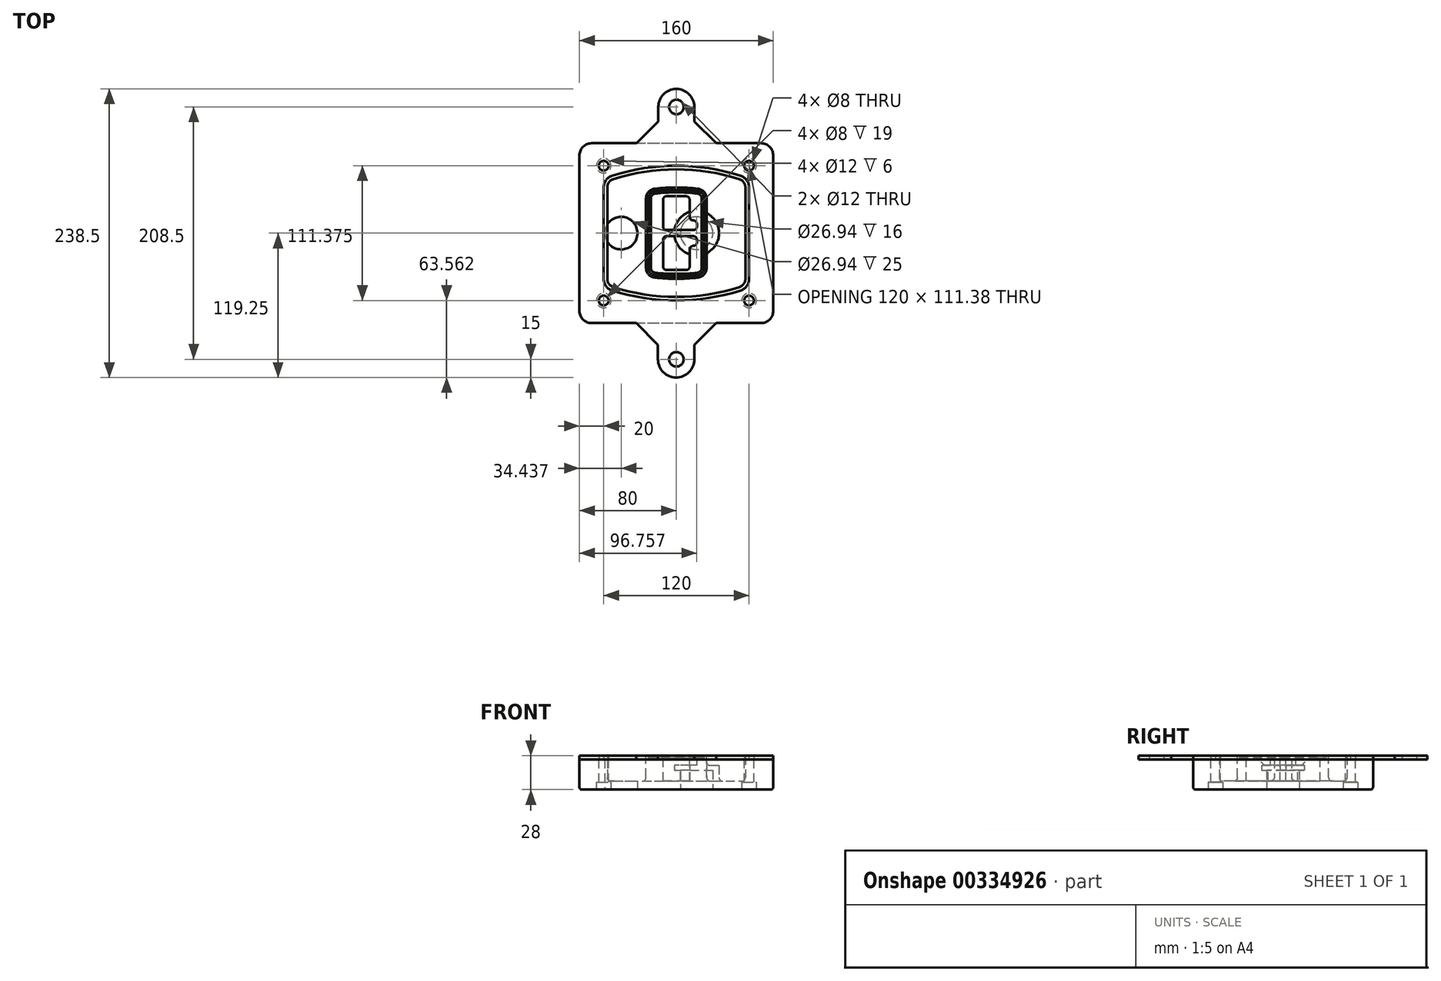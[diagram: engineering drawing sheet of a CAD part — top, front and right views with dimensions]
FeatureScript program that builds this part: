
annotation { "Feature Type Name" : "Feature", "Feature Type Description" : "" }
export const myFeature = defineFeature(function(context is Context, id is Id, definition is map)
    precondition{}
    {
        {
            var Q0;
            Q0=qCreatedBy(makeId("Top.planeOp"),FACE);
            var sketch = newSketch(context, id + "F0", { "sketchPlane" : qUnion([Q0])});
            skPoint(sketch, "E0.rect.middle", {"position": v(0, 0) * mm});
            skLineSegment(sketch, "E1.bottom", {"start": v(-70, -74.25) * mm, "end": v(70, -74.25) * mm});
            skLineSegment(sketch, "E1.top", {"start": v(-70, 74.25) * mm, "end": v(70, 74.25) * mm});
            skLineSegment(sketch, "E1.left", {"start": v(-80, -64.25) * mm, "end": v(-80, 64.25) * mm});
            skLineSegment(sketch, "E1.right", {"start": v(80, -64.25) * mm, "end": v(80, 64.25) * mm});
            skLineSegment(sketch, "E2", {"start": v(-80, 74.25) * mm, "end": v(80, -74.25) * mm, "construction": true});
            skLineSegment(sketch, "E3", {"start": v(80, 74.25) * mm, "end": v(-80, -74.25) * mm, "construction": true});
            skCircle(sketch, "E4", {"center": v(-60, 55.69) * mm, "radius": 4 * mm});
            skCircle(sketch, "E5", {"center": v(60, 55.69) * mm, "radius": 4 * mm});
            skCircle(sketch, "E6", {"center": v(60, -55.69) * mm, "radius": 4 * mm});
            skCircle(sketch, "E7", {"center": v(-60, -55.69) * mm, "radius": 4 * mm});
            skLineSegment(sketch, "E8", {"start": v(-60, 55.69) * mm, "end": v(60, 55.69) * mm, "construction": true});
            skLineSegment(sketch, "E9", {"start": v(60, 55.69) * mm, "end": v(60, -55.69) * mm, "construction": true});
            skLineSegment(sketch, "E10", {"start": v(60, -55.69) * mm, "end": v(-60, -55.69) * mm, "construction": true});
            skLineSegment(sketch, "E11", {"start": v(-60, -55.69) * mm, "end": v(-60, 55.69) * mm, "construction": true});
            skLineSegment(sketch, "E12", {"start": v(-60, 37.87) * mm, "end": v(-60, -37.87) * mm});
            skLineSegment(sketch, "E13", {"start": v(60, 37.87) * mm, "end": v(60, -37.87) * mm});
            skArc(sketch, "E14", {"start": v(53.05, 47.4) * mm, "mid": v(0, 55.69) * mm, "end": v(-53.05, 47.4) * mm});
            skArc(sketch, "E15", {"start": v(-53.05, -47.4) * mm, "mid": v(0, -55.69) * mm, "end": v(53.05, -47.4) * mm});
            skLineSegment(sketch, "E16", {"start": v(-60, 0) * mm, "end": v(60, 0) * mm, "construction": true});
            skPoint(sketch, "E17.visualSharp", {"position": v(-60, -45) * mm});
            skArc(sketch, "E17.filletArc", {"start": v(-60, -37.87) * mm, "mid": v(-58.08, -43.76) * mm, "end": v(-53.05, -47.4) * mm});
            skPoint(sketch, "E18.visualSharp", {"position": v(-60, 45) * mm});
            skArc(sketch, "E18.filletArc", {"start": v(-53.05, 47.4) * mm, "mid": v(-58.08, 43.76) * mm, "end": v(-60, 37.87) * mm});
            skPoint(sketch, "E19.visualSharp", {"position": v(60, 45) * mm});
            skArc(sketch, "E19.filletArc", {"start": v(60, 37.87) * mm, "mid": v(58.08, 43.76) * mm, "end": v(53.05, 47.4) * mm});
            skPoint(sketch, "E20.visualSharp", {"position": v(60, -45) * mm});
            skArc(sketch, "E20.filletArc", {"start": v(53.05, -47.4) * mm, "mid": v(58.08, -43.76) * mm, "end": v(60, -37.87) * mm});
            skPoint(sketch, "E21.visualSharp", {"position": v(-80, 74.25) * mm});
            skArc(sketch, "E21.filletArc", {"start": v(-70, 74.25) * mm, "mid": v(-77.07, 71.32) * mm, "end": v(-80, 64.25) * mm});
            skPoint(sketch, "E22.visualSharp", {"position": v(80, 74.25) * mm});
            skArc(sketch, "E22.filletArc", {"start": v(80, 64.25) * mm, "mid": v(77.07, 71.32) * mm, "end": v(70, 74.25) * mm});
            skPoint(sketch, "E23.visualSharp", {"position": v(80, -74.25) * mm});
            skArc(sketch, "E23.filletArc", {"start": v(70, -74.25) * mm, "mid": v(77.07, -71.32) * mm, "end": v(80, -64.25) * mm});
            skPoint(sketch, "E24.visualSharp", {"position": v(-80, -74.25) * mm});
            skArc(sketch, "E24.filletArc", {"start": v(-80, -64.25) * mm, "mid": v(-77.07, -71.32) * mm, "end": v(-70, -74.25) * mm});
            skArc(sketch, "E25.0", {"start": v(57, 37.87) * mm, "mid": v(55.66, 42) * mm, "end": v(52.14, 44.53) * mm});
            skLineSegment(sketch, "E25.1", {"start": v(57, 37.87) * mm, "end": v(57, -37.87) * mm});
            skArc(sketch, "E25.2", {"start": v(52.14, -44.53) * mm, "mid": v(55.66, -42) * mm, "end": v(57, -37.87) * mm});
            skArc(sketch, "E25.3", {"start": v(-52.14, -44.53) * mm, "mid": v(0, -52.69) * mm, "end": v(52.14, -44.53) * mm});
            skArc(sketch, "E25.4", {"start": v(-57, -37.87) * mm, "mid": v(-55.66, -42) * mm, "end": v(-52.14, -44.53) * mm});
            skArc(sketch, "E25.5", {"start": v(52.14, 44.53) * mm, "mid": v(0, 52.69) * mm, "end": v(-52.14, 44.53) * mm});
            skLineSegment(sketch, "E25.6", {"start": v(-57, 37.87) * mm, "end": v(-57, -37.87) * mm});
            skArc(sketch, "E25.7", {"start": v(-52.14, 44.53) * mm, "mid": v(-55.66, 42) * mm, "end": v(-57, 37.87) * mm});
            skArc(sketch, "E26.0", {"start": v(-54.27, 51.2) * mm, "mid": v(-61.31, 46.12) * mm, "end": v(-64, 37.87) * mm});
            skArc(sketch, "E26.1", {"start": v(54.27, 51.2) * mm, "mid": v(0, 59.69) * mm, "end": v(-54.27, 51.2) * mm});
            skArc(sketch, "E26.2", {"start": v(64, 37.87) * mm, "mid": v(61.31, 46.12) * mm, "end": v(54.27, 51.2) * mm});
            skLineSegment(sketch, "E26.3", {"start": v(64, 37.87) * mm, "end": v(64, -37.87) * mm});
            skArc(sketch, "E26.4", {"start": v(54.27, -51.2) * mm, "mid": v(61.31, -46.12) * mm, "end": v(64, -37.87) * mm});
            skLineSegment(sketch, "E26.5", {"start": v(-64, 37.87) * mm, "end": v(-64, -37.87) * mm});
            skArc(sketch, "E26.6", {"start": v(-54.27, -51.2) * mm, "mid": v(0, -59.69) * mm, "end": v(54.27, -51.2) * mm});
            skArc(sketch, "E26.7", {"start": v(-64, -37.87) * mm, "mid": v(-61.31, -46.12) * mm, "end": v(-54.27, -51.2) * mm});
            skSolve(sketch);
        }
        {
            var Q0;
            Q0=makeQuery(id+"F0.imprint","IMPRINT",FACE,{"disambiguationData":[TD([[makeQuery(id+"F0.imprint","IMPRINT",EDGE,{"derivedFrom":sQuery(id+"F0.wireOp",EDGE,"E1.bottom")}),1.0]])]});
            var Q1;
            Q1=makeQuery(id+"F0.imprint","IMPRINT",FACE,{"disambiguationData":[TD([[makeQuery(id+"F0.imprint","IMPRINT",EDGE,{"derivedFrom":sQuery(id+"F0.wireOp",EDGE,"E12")}),1.0]])]});
            var Q2;
            Q2=makeQuery(id+"F0.imprint","IMPRINT",FACE,{"disambiguationData":[TD([[makeQuery(id+"F0.imprint","IMPRINT",EDGE,{"derivedFrom":sQuery(id+"F0.wireOp",EDGE,"E25.0")}),1.0]])]});
            var Q3;
            Q3=makeQuery(id+"F0.imprint","IMPRINT",FACE,{"disambiguationData":[TD([[makeQuery(id+"F0.imprint","IMPRINT",EDGE,{"derivedFrom":sQuery(id+"F0.wireOp",EDGE,"E12")}),-1.0]])]});
            extrude(context, id + "F1", {"entities" : qUnion([Q0, Q1, Q2, Q3]), "oppositeDirection" : true, "depth" : 25 * mm});
        }
        {
            var Q0;
            Q0=makeQuery(id+"F0.imprint","IMPRINT",FACE,{"disambiguationData":[TD([[makeQuery(id+"F0.imprint","IMPRINT",EDGE,{"derivedFrom":sQuery(id+"F0.wireOp",EDGE,"E12")}),1.0]])]});
            extrude(context, id + "F2", {"entities" : qUnion([Q0]), "operationType" : NewBodyOperationType.ADD, "depth" : 3 * mm});
        }
        {
            var Q0;
            Q0=makeQuery(id+"F0.imprint","IMPRINT",FACE,{"disambiguationData":[TD([[makeQuery(id+"F0.imprint","IMPRINT",EDGE,{"derivedFrom":sQuery(id+"F0.wireOp",EDGE,"E25.0")}),1.0]])]});
            extrude(context, id + "F3", {"entities" : qUnion([Q0]), "operationType" : NewBodyOperationType.REMOVE, "oppositeDirection" : true, "depth" : 18 * mm});
        }
        {
            var Q0;
            Q0=makeQuery(id+"F2.opExtrude","CAP_FACE",FACE,{"disambiguationData":[OSD([sQuery(id+"F0.wireOp",EDGE,"E12"),sQuery(id+"F0.wireOp",EDGE,"E13"),sQuery(id+"F0.wireOp",EDGE,"E14"),sQuery(id+"F0.wireOp",EDGE,"E15"),sQuery(id+"F0.wireOp",EDGE,"E17.filletArc"),sQuery(id+"F0.wireOp",EDGE,"E18.filletArc"),sQuery(id+"F0.wireOp",EDGE,"E19.filletArc"),sQuery(id+"F0.wireOp",EDGE,"E20.filletArc"),sQuery(id+"F0.wireOp",EDGE,"E25.0"),sQuery(id+"F0.wireOp",EDGE,"E25.1"),sQuery(id+"F0.wireOp",EDGE,"E25.2"),sQuery(id+"F0.wireOp",EDGE,"E25.3"),sQuery(id+"F0.wireOp",EDGE,"E25.4"),sQuery(id+"F0.wireOp",EDGE,"E25.5"),sQuery(id+"F0.wireOp",EDGE,"E25.6"),sQuery(id+"F0.wireOp",EDGE,"E25.7")])],"isStart":false});
            var sketch = newSketch(context, id + "F4", { "sketchPlane" : qUnion([Q0])});
            skArc(sketch, "E27.0", {"start": v(-17.92, -36.65) * mm, "mid": v(0, -37.69) * mm, "end": v(17.92, -36.65) * mm});
            skArc(sketch, "E28.0", {"start": v(17.92, 36.65) * mm, "mid": v(0, 37.69) * mm, "end": v(-17.92, 36.65) * mm});
            skLineSegment(sketch, "E29", {"start": v(-25, 28.7) * mm, "end": v(-25, -28.7) * mm});
            skLineSegment(sketch, "E30", {"start": v(25, 28.7) * mm, "end": v(25, -28.7) * mm});
            skLineSegment(sketch, "E31", {"start": v(-25, 35.67) * mm, "end": v(25, 35.67) * mm, "construction": true});
            skLineSegment(sketch, "E32", {"start": v(-25, -35.67) * mm, "end": v(25, -35.67) * mm, "construction": true});
            skPoint(sketch, "E33.visualSharp", {"position": v(-25, 35.67) * mm});
            skArc(sketch, "E33.filletArc", {"start": v(-17.92, 36.65) * mm, "mid": v(-22.97, 34.03) * mm, "end": v(-25, 28.7) * mm});
            skPoint(sketch, "E34.visualSharp", {"position": v(25, 35.67) * mm});
            skArc(sketch, "E34.filletArc", {"start": v(25, 28.7) * mm, "mid": v(22.97, 34.03) * mm, "end": v(17.92, 36.65) * mm});
            skPoint(sketch, "E35.visualSharp", {"position": v(25, -35.67) * mm});
            skArc(sketch, "E35.filletArc", {"start": v(17.92, -36.65) * mm, "mid": v(22.97, -34.03) * mm, "end": v(25, -28.7) * mm});
            skPoint(sketch, "E36.visualSharp", {"position": v(-25, -35.67) * mm});
            skArc(sketch, "E36.filletArc", {"start": v(-25, -28.7) * mm, "mid": v(-22.97, -34.03) * mm, "end": v(-17.92, -36.65) * mm});
            skArc(sketch, "E37.0", {"start": v(52.14, 44.53) * mm, "mid": v(0, 52.69) * mm, "end": v(-52.14, 44.53) * mm});
            skArc(sketch, "E37.1", {"start": v(-52.14, 44.53) * mm, "mid": v(-55.66, 42) * mm, "end": v(-57, 37.87) * mm});
            skLineSegment(sketch, "E37.2", {"start": v(-57, 37.87) * mm, "end": v(-57, -37.87) * mm});
            skArc(sketch, "E37.3", {"start": v(-57, -37.87) * mm, "mid": v(-55.66, -42) * mm, "end": v(-52.14, -44.53) * mm});
            skArc(sketch, "E37.4", {"start": v(-52.14, -44.53) * mm, "mid": v(0, -52.69) * mm, "end": v(52.14, -44.53) * mm});
            skArc(sketch, "E37.5", {"start": v(52.14, -44.53) * mm, "mid": v(55.66, -42) * mm, "end": v(57, -37.87) * mm});
            skLineSegment(sketch, "E37.6", {"start": v(57, 37.87) * mm, "end": v(57, -37.87) * mm});
            skArc(sketch, "E37.7", {"start": v(57, 37.87) * mm, "mid": v(55.66, 42) * mm, "end": v(52.14, 44.53) * mm});
            skLineSegment(sketch, "E38.0", {"start": v(23, 28.7) * mm, "end": v(23, -28.7) * mm});
            skArc(sketch, "E38.1", {"start": v(17.7, -34.67) * mm, "mid": v(21.48, -32.7) * mm, "end": v(23, -28.7) * mm});
            skArc(sketch, "E38.2", {"start": v(-17.7, -34.67) * mm, "mid": v(0, -35.69) * mm, "end": v(17.7, -34.67) * mm});
            skArc(sketch, "E38.3", {"start": v(-23, -28.7) * mm, "mid": v(-21.48, -32.7) * mm, "end": v(-17.7, -34.67) * mm});
            skLineSegment(sketch, "E38.4", {"start": v(-23, 28.7) * mm, "end": v(-23, -28.7) * mm});
            skArc(sketch, "E38.5", {"start": v(23, 28.7) * mm, "mid": v(21.48, 32.7) * mm, "end": v(17.7, 34.67) * mm});
            skArc(sketch, "E38.6", {"start": v(-17.7, 34.67) * mm, "mid": v(-21.48, 32.7) * mm, "end": v(-23, 28.7) * mm});
            skArc(sketch, "E38.7", {"start": v(17.7, 34.67) * mm, "mid": v(0, 35.69) * mm, "end": v(-17.7, 34.67) * mm});
            skArc(sketch, "E39.0", {"start": v(21, 28.7) * mm, "mid": v(19.99, 31.37) * mm, "end": v(17.46, 32.68) * mm});
            skLineSegment(sketch, "E39.1", {"start": v(21, 28.7) * mm, "end": v(21, -28.7) * mm});
            skArc(sketch, "E39.2", {"start": v(17.46, -32.68) * mm, "mid": v(19.99, -31.37) * mm, "end": v(21, -28.7) * mm});
            skArc(sketch, "E39.3", {"start": v(-17.46, -32.68) * mm, "mid": v(0, -33.69) * mm, "end": v(17.46, -32.68) * mm});
            skArc(sketch, "E39.4", {"start": v(-21, -28.7) * mm, "mid": v(-19.99, -31.37) * mm, "end": v(-17.46, -32.68) * mm});
            skArc(sketch, "E39.5", {"start": v(17.46, 32.68) * mm, "mid": v(0, 33.69) * mm, "end": v(-17.46, 32.68) * mm});
            skLineSegment(sketch, "E39.6", {"start": v(-21, 28.7) * mm, "end": v(-21, -28.7) * mm});
            skArc(sketch, "E39.7", {"start": v(-17.46, 32.68) * mm, "mid": v(-19.99, 31.37) * mm, "end": v(-21, 28.7) * mm});
            skLineSegment(sketch, "E40", {"start": v(-25, 0) * mm, "end": v(25, 0) * mm, "construction": true});
            skLineSegment(sketch, "E41", {"start": v(-11, 5.5) * mm, "end": v(-11, 27.5) * mm});
            skLineSegment(sketch, "E42", {"start": v(-8, 30.5) * mm, "end": v(8, 30.5) * mm});
            skLineSegment(sketch, "E43", {"start": v(11, 27.5) * mm, "end": v(11, 13.5) * mm});
            skLineSegment(sketch, "E44", {"start": v(14, 10.5) * mm, "end": v(14, 10.5) * mm});
            skLineSegment(sketch, "E45", {"start": v(17, 7.5) * mm, "end": v(17, 5.5) * mm});
            skLineSegment(sketch, "E46", {"start": v(14, 2.5) * mm, "end": v(-8, 2.5) * mm});
            skPoint(sketch, "E47.visualSharp", {"position": v(-11, 30.5) * mm});
            skArc(sketch, "E47.filletArc", {"start": v(-8, 30.5) * mm, "mid": v(-10.12, 29.62) * mm, "end": v(-11, 27.5) * mm});
            skPoint(sketch, "E48.visualSharp", {"position": v(11, 30.5) * mm});
            skArc(sketch, "E48.filletArc", {"start": v(11, 27.5) * mm, "mid": v(10.12, 29.62) * mm, "end": v(8, 30.5) * mm});
            skPoint(sketch, "E49.visualSharp", {"position": v(11, 10.5) * mm});
            skArc(sketch, "E49.filletArc", {"start": v(11, 13.5) * mm, "mid": v(11.88, 11.38) * mm, "end": v(14, 10.5) * mm});
            skPoint(sketch, "E50.visualSharp", {"position": v(17, 10.5) * mm});
            skArc(sketch, "E50.filletArc", {"start": v(17, 7.5) * mm, "mid": v(16.12, 9.62) * mm, "end": v(14, 10.5) * mm});
            skPoint(sketch, "E51.visualSharp", {"position": v(17, 2.5) * mm});
            skArc(sketch, "E51.filletArc", {"start": v(14, 2.5) * mm, "mid": v(16.12, 3.38) * mm, "end": v(17, 5.5) * mm});
            skPoint(sketch, "E52.visualSharp", {"position": v(-11, 2.5) * mm});
            skArc(sketch, "E52.filletArc", {"start": v(-11, 5.5) * mm, "mid": v(-10.12, 3.38) * mm, "end": v(-8, 2.5) * mm});
            skLineSegment(sketch, "E53.0.MirrorCS", {"start": v(14, -2.5) * mm, "end": v(-8, -2.5) * mm});
            skArc(sketch, "E54.0.MirrorCS", {"start": v(-11, -5.5) * mm, "mid": v(-10.12, -3.38) * mm, "end": v(-8, -2.5) * mm});
            skLineSegment(sketch, "E55.0.MirrorCS", {"start": v(-11, -5.5) * mm, "end": v(-11, -27.5) * mm});
            skArc(sketch, "E56.0.MirrorCS", {"start": v(-8, -30.5) * mm, "mid": v(-10.12, -29.62) * mm, "end": v(-11, -27.5) * mm});
            skLineSegment(sketch, "E57.0.MirrorCS", {"start": v(-8, -30.5) * mm, "end": v(8, -30.5) * mm});
            skArc(sketch, "E58.0.MirrorCS", {"start": v(11, -27.5) * mm, "mid": v(10.12, -29.62) * mm, "end": v(8, -30.5) * mm});
            skLineSegment(sketch, "E59.0.MirrorCS", {"start": v(11, -27.5) * mm, "end": v(11, -13.5) * mm});
            skArc(sketch, "E60.0.MirrorCS", {"start": v(11, -13.5) * mm, "mid": v(11.88, -11.38) * mm, "end": v(14, -10.5) * mm});
            skArc(sketch, "E61.0.MirrorCS", {"start": v(17, -7.5) * mm, "mid": v(16.12, -9.62) * mm, "end": v(14, -10.5) * mm});
            skLineSegment(sketch, "E62.0.MirrorCS", {"start": v(17, -7.5) * mm, "end": v(17, -5.5) * mm});
            skArc(sketch, "E63.0.MirrorCS", {"start": v(14, -2.5) * mm, "mid": v(16.12, -3.38) * mm, "end": v(17, -5.5) * mm});
            skSolve(sketch);
        }
        {
            var Q0;
            Q0=makeQuery(id+"F4.imprint","IMPRINT",FACE,{"disambiguationData":[TD([[makeQuery(id+"F4.imprint","IMPRINT",EDGE,{"derivedFrom":sQuery(id+"F4.wireOp",EDGE,"E27.0")}),1.0]])]});
            var Q1;
            Q1=makeQuery(id+"F4.imprint","IMPRINT",FACE,{"disambiguationData":[TD([[makeQuery(id+"F4.imprint","IMPRINT",EDGE,{"derivedFrom":sQuery(id+"F4.wireOp",EDGE,"E38.0")}),-1.0]])]});
            var Q2;
            Q2=makeQuery(id+"F4.imprint","IMPRINT",FACE,{"disambiguationData":[TD([[makeQuery(id+"F4.imprint","IMPRINT",EDGE,{"derivedFrom":sQuery(id+"F4.wireOp",EDGE,"E39.0")}),1.0]])]});
            extrude(context, id + "F5", {"entities" : qUnion([Q0, Q1, Q2]), "operationType" : NewBodyOperationType.ADD, "endBound" : BoundingType.UP_TO_NEXT, "oppositeDirection" : true, "depth" : 25 * mm});
        }
        {
            var Q0;
            Q0=makeQuery(id+"F4.imprint","IMPRINT",FACE,{"disambiguationData":[TD([[makeQuery(id+"F4.imprint","IMPRINT",EDGE,{"derivedFrom":sQuery(id+"F4.wireOp",EDGE,"E38.0")}),-1.0]])]});
            extrude(context, id + "F6", {"entities" : qUnion([Q0]), "operationType" : NewBodyOperationType.REMOVE, "oppositeDirection" : true, "depth" : 2 * mm});
        }
        {
            var Q0;
            Q0=makeQuery(id+"F1.opExtrude","CAP_FACE",FACE,{"disambiguationData":[OSD([sQuery(id+"F0.wireOp",EDGE,"E1.bottom"),sQuery(id+"F0.wireOp",EDGE,"E1.top"),sQuery(id+"F0.wireOp",EDGE,"E1.left"),sQuery(id+"F0.wireOp",EDGE,"E1.right"),sQuery(id+"F0.wireOp",EDGE,"E4"),sQuery(id+"F0.wireOp",EDGE,"E5"),sQuery(id+"F0.wireOp",EDGE,"E6"),sQuery(id+"F0.wireOp",EDGE,"E7"),sQuery(id+"F0.wireOp",EDGE,"E21.filletArc"),sQuery(id+"F0.wireOp",EDGE,"E22.filletArc"),sQuery(id+"F0.wireOp",EDGE,"E23.filletArc"),sQuery(id+"F0.wireOp",EDGE,"E24.filletArc")])],"isStart":false});
            var sketch = newSketch(context, id + "F7", { "sketchPlane" : qUnion([Q0])});
            skCircle(sketch, "E64", {"center": v(16.76, 0) * mm, "radius": 13.47 * mm});
            skCircle(sketch, "E65", {"center": v(-45.56, 0) * mm, "radius": 13.47 * mm});
            skLineSegment(sketch, "E66", {"start": v(80, 0) * mm, "end": v(-80, 0) * mm});
            skCircle(sketch, "E67", {"center": v(16.76, 0) * mm, "radius": 18.47 * mm});
            skCircle(sketch, "E68", {"center": v(60, -55.69) * mm, "radius": 6 * mm});
            skCircle(sketch, "E69", {"center": v(-60, -55.69) * mm, "radius": 6 * mm});
            skCircle(sketch, "E70", {"center": v(-60, 55.69) * mm, "radius": 6 * mm});
            skCircle(sketch, "E71", {"center": v(60, 55.69) * mm, "radius": 6 * mm});
            skSolve(sketch);
        }
        {
            var Q0;
            {var subQ1=sQuery(id+"F7.wireOp",EDGE,"E66");var subQ4=sQuery(id+"F7.wireOp",EDGE,"E64");var subQ6=makeQuery(id+"F7.imprint","INTERSECT",VERTEX,{"disambiguationData":[OD(0.0)],"derivedFrom":[subQ4,subQ1]});Q0=makeQuery(id+"F7.imprint","IMPRINT",FACE,{"disambiguationData":[TD([[makeQuery(id+"F7.imprint","IMPRINT",EDGE,{"disambiguationData":[TD([[subQ6,-1.0]])],"derivedFrom":subQ4}),-1.0]])]});}
            var Q1;
            {var subQ0=sQuery(id+"F7.wireOp",EDGE,"E66");var subQ1=sQuery(id+"F7.wireOp",EDGE,"E64");var subQ3=makeQuery(id+"F7.imprint","INTERSECT",VERTEX,{"disambiguationData":[OD(0.0)],"derivedFrom":[subQ1,subQ0]});Q1=makeQuery(id+"F7.imprint","IMPRINT",FACE,{"disambiguationData":[TD([[makeQuery(id+"F7.imprint","IMPRINT",EDGE,{"disambiguationData":[TD([[subQ3,-1.0]])],"derivedFrom":subQ1}),1.0]])]});}
            var Q2;
            {var subQ0=sQuery(id+"F7.wireOp",EDGE,"E66");var subQ1=sQuery(id+"F7.wireOp",EDGE,"E64");var subQ3=makeQuery(id+"F7.imprint","INTERSECT",VERTEX,{"disambiguationData":[OD(0.0)],"derivedFrom":[subQ1,subQ0]});Q2=makeQuery(id+"F7.imprint","IMPRINT",FACE,{"disambiguationData":[TD([[makeQuery(id+"F7.imprint","IMPRINT",EDGE,{"disambiguationData":[TD([[subQ3,1.0]])],"derivedFrom":subQ1}),1.0]])]});}
            var Q3;
            {var subQ1=sQuery(id+"F7.wireOp",EDGE,"E66");var subQ4=sQuery(id+"F7.wireOp",EDGE,"E64");var subQ6=makeQuery(id+"F7.imprint","INTERSECT",VERTEX,{"disambiguationData":[OD(0.0)],"derivedFrom":[subQ4,subQ1]});Q3=makeQuery(id+"F7.imprint","IMPRINT",FACE,{"disambiguationData":[TD([[makeQuery(id+"F7.imprint","IMPRINT",EDGE,{"disambiguationData":[TD([[subQ6,1.0]])],"derivedFrom":subQ4}),-1.0]])]});}
            extrude(context, id + "F8", {"entities" : qUnion([Q0, Q1, Q2, Q3]), "operationType" : NewBodyOperationType.ADD, "oppositeDirection" : true, "depth" : 20 * mm});
        }
        {
            var Q0;
            {var subQ0=sQuery(id+"F7.wireOp",EDGE,"E66");var subQ1=sQuery(id+"F7.wireOp",EDGE,"E64");var subQ3=makeQuery(id+"F7.imprint","INTERSECT",VERTEX,{"disambiguationData":[OD(0.0)],"derivedFrom":[subQ1,subQ0]});Q0=makeQuery(id+"F7.imprint","IMPRINT",FACE,{"disambiguationData":[TD([[makeQuery(id+"F7.imprint","IMPRINT",EDGE,{"disambiguationData":[TD([[subQ3,-1.0]])],"derivedFrom":subQ1}),1.0]])]});}
            var Q1;
            {var subQ0=sQuery(id+"F7.wireOp",EDGE,"E66");var subQ1=sQuery(id+"F7.wireOp",EDGE,"E64");var subQ3=makeQuery(id+"F7.imprint","INTERSECT",VERTEX,{"disambiguationData":[OD(0.0)],"derivedFrom":[subQ1,subQ0]});Q1=makeQuery(id+"F7.imprint","IMPRINT",FACE,{"disambiguationData":[TD([[makeQuery(id+"F7.imprint","IMPRINT",EDGE,{"disambiguationData":[TD([[subQ3,1.0]])],"derivedFrom":subQ1}),1.0]])]});}
            extrude(context, id + "F9", {"entities" : qUnion([Q0, Q1]), "operationType" : NewBodyOperationType.REMOVE, "oppositeDirection" : true, "depth" : 16 * mm});
        }
        {
            var Q0;
            {var subQ0=sQuery(id+"F7.wireOp",EDGE,"E66");var subQ1=sQuery(id+"F7.wireOp",EDGE,"E65");var subQ3=makeQuery(id+"F7.imprint","INTERSECT",VERTEX,{"disambiguationData":[OD(0.0)],"derivedFrom":[subQ1,subQ0]});Q0=makeQuery(id+"F7.imprint","IMPRINT",FACE,{"disambiguationData":[TD([[makeQuery(id+"F7.imprint","IMPRINT",EDGE,{"disambiguationData":[TD([[subQ3,-1.0]])],"derivedFrom":subQ1}),1.0]])]});}
            var Q1;
            {var subQ0=sQuery(id+"F7.wireOp",EDGE,"E66");var subQ1=sQuery(id+"F7.wireOp",EDGE,"E65");var subQ3=makeQuery(id+"F7.imprint","INTERSECT",VERTEX,{"disambiguationData":[OD(0.0)],"derivedFrom":[subQ1,subQ0]});Q1=makeQuery(id+"F7.imprint","IMPRINT",FACE,{"disambiguationData":[TD([[makeQuery(id+"F7.imprint","IMPRINT",EDGE,{"disambiguationData":[TD([[subQ3,1.0]])],"derivedFrom":subQ1}),1.0]])]});}
            extrude(context, id + "F10", {"entities" : qUnion([Q0, Q1]), "operationType" : NewBodyOperationType.REMOVE, "oppositeDirection" : true, "depth" : 25 * mm});
        }
        {
            var Q0;
            Q0=makeQuery(id+"F7.imprint","IMPRINT",FACE,{"disambiguationData":[TD([[makeQuery(id+"F7.imprint","IMPRINT",EDGE,{"derivedFrom":sQuery(id+"F7.wireOp",EDGE,"E68")}),1.0]])]});
            var Q1;
            Q1=makeQuery(id+"F7.imprint","IMPRINT",FACE,{"disambiguationData":[TD([[makeQuery(id+"F7.imprint","IMPRINT",EDGE,{"derivedFrom":makeQuery(id+"F1.opExtrude","CAP_EDGE",EDGE,{"disambiguationData":[OSD([sQuery(id+"F0.wireOp",EDGE,"E5")])],"isStart":false})}),-1.0]])]});
            var Q2;
            Q2=makeQuery(id+"F7.imprint","IMPRINT",FACE,{"disambiguationData":[TD([[makeQuery(id+"F7.imprint","IMPRINT",EDGE,{"derivedFrom":sQuery(id+"F7.wireOp",EDGE,"E69")}),1.0]])]});
            var Q3;
            Q3=makeQuery(id+"F7.imprint","IMPRINT",FACE,{"disambiguationData":[TD([[makeQuery(id+"F7.imprint","IMPRINT",EDGE,{"derivedFrom":makeQuery(id+"F1.opExtrude","CAP_EDGE",EDGE,{"disambiguationData":[OSD([sQuery(id+"F0.wireOp",EDGE,"E4")])],"isStart":false})}),-1.0]])]});
            var Q4;
            Q4=makeQuery(id+"F7.imprint","IMPRINT",FACE,{"disambiguationData":[TD([[makeQuery(id+"F7.imprint","IMPRINT",EDGE,{"derivedFrom":sQuery(id+"F7.wireOp",EDGE,"E70")}),1.0]])]});
            var Q5;
            Q5=makeQuery(id+"F7.imprint","IMPRINT",FACE,{"disambiguationData":[TD([[makeQuery(id+"F7.imprint","IMPRINT",EDGE,{"derivedFrom":makeQuery(id+"F1.opExtrude","CAP_EDGE",EDGE,{"disambiguationData":[OSD([sQuery(id+"F0.wireOp",EDGE,"E7")])],"isStart":false})}),-1.0]])]});
            var Q6;
            Q6=makeQuery(id+"F7.imprint","IMPRINT",FACE,{"disambiguationData":[TD([[makeQuery(id+"F7.imprint","IMPRINT",EDGE,{"derivedFrom":sQuery(id+"F7.wireOp",EDGE,"E71")}),1.0]])]});
            var Q7;
            Q7=makeQuery(id+"F7.imprint","IMPRINT",FACE,{"disambiguationData":[TD([[makeQuery(id+"F7.imprint","IMPRINT",EDGE,{"derivedFrom":makeQuery(id+"F1.opExtrude","CAP_EDGE",EDGE,{"disambiguationData":[OSD([sQuery(id+"F0.wireOp",EDGE,"E6")])],"isStart":false})}),-1.0]])]});
            extrude(context, id + "F11", {"entities" : qUnion([Q0, Q1, Q2, Q3, Q4, Q5, Q6, Q7]), "operationType" : NewBodyOperationType.REMOVE, "oppositeDirection" : true, "depth" : 6 * mm});
        }
        {
            var Q0;
            Q0=makeQuery(id+"F9.boolean.opBoolean","COPY",FACE,{"derivedFrom":makeQuery(id+"F9.opExtrude","CAP_FACE",FACE,{"disambiguationData":[OSD([sQuery(id+"F7.wireOp",EDGE,"E64")])],"isStart":false})});
            var sketch = newSketch(context, id + "F12", { "sketchPlane" : qUnion([Q0])});
            skArc(sketch, "E72.0", {"start": v(11, 17.55) * mm, "mid": v(2.57, 11.82) * mm, "end": v(-1.54, 2.5) * mm});
            skArc(sketch, "E72.1", {"start": v(-1.54, -2.5) * mm, "mid": v(2.57, -11.82) * mm, "end": v(11, -17.55) * mm});
            skLineSegment(sketch, "E73", {"start": v(-1.54, -2.5) * mm, "end": v(14, -2.5) * mm});
            skLineSegment(sketch, "E74.0", {"start": v(14, 2.5) * mm, "end": v(-1.54, 2.5) * mm});
            skArc(sketch, "E74.1", {"start": v(14, 2.5) * mm, "mid": v(16.12, 3.38) * mm, "end": v(17, 5.5) * mm});
            skLineSegment(sketch, "E74.2", {"start": v(17, 7.5) * mm, "end": v(17, 5.5) * mm});
            skArc(sketch, "E74.3", {"start": v(17, 7.5) * mm, "mid": v(16.12, 9.62) * mm, "end": v(14, 10.5) * mm});
            skArc(sketch, "E74.4", {"start": v(11, 13.5) * mm, "mid": v(11.88, 11.38) * mm, "end": v(14, 10.5) * mm});
            skLineSegment(sketch, "E74.5", {"start": v(11, 17.55) * mm, "end": v(11, 13.5) * mm});
            skLineSegment(sketch, "E74.7", {"start": v(14, -2.5) * mm, "end": v(-1.54, -2.5) * mm});
            skArc(sketch, "E74.8", {"start": v(14, -2.5) * mm, "mid": v(16.12, -3.38) * mm, "end": v(17, -5.5) * mm});
            skLineSegment(sketch, "E74.9", {"start": v(17, -7.5) * mm, "end": v(17, -5.5) * mm});
            skArc(sketch, "E74.10", {"start": v(17, -7.5) * mm, "mid": v(16.12, -9.62) * mm, "end": v(14, -10.5) * mm});
            skArc(sketch, "E74.11", {"start": v(11, -13.5) * mm, "mid": v(11.88, -11.38) * mm, "end": v(14, -10.5) * mm});
            skLineSegment(sketch, "E74.12", {"start": v(11, -17.55) * mm, "end": v(11, -13.5) * mm});
            skPoint(sketch, "E75.orphan", {"position": v(11, -27.5) * mm});
            skPoint(sketch, "E76.orphan", {"position": v(-8, -2.5) * mm});
            skPoint(sketch, "E77.orphan", {"position": v(-8, 2.5) * mm});
            skPoint(sketch, "E78.orphan", {"position": v(11, 27.5) * mm});
            skSolve(sketch);
        }
        {
            var Q0;
            {var subQ7=sQuery(id+"F12.wireOp",EDGE,"E72.0");var subQ14=sQuery(id+"F12.wireOp",EDGE,"E72.1");var subQ16=sQuery(id+"F12.wireOp",EDGE,"E74.1");var subQ18=sQuery(id+"F12.wireOp",EDGE,"E74.8");Q0=qUnion([makeQuery(id+"F12.imprint","IMPRINT",FACE,{"disambiguationData":[TD([[makeQuery(id+"F12.imprint","IMPRINT",EDGE,{"derivedFrom":subQ7}),1.0]])]}),makeQuery(id+"F12.imprint","IMPRINT",FACE,{"disambiguationData":[TD([[makeQuery(id+"F12.imprint","IMPRINT",EDGE,{"derivedFrom":subQ14}),1.0]])]}),makeQuery(id+"F12.imprint","IMPRINT",FACE,{"disambiguationData":[TD([[makeQuery(id+"F12.imprint","IMPRINT",EDGE,{"derivedFrom":subQ16}),1.0]])]}),makeQuery(id+"F12.imprint","IMPRINT",FACE,{"disambiguationData":[TD([[makeQuery(id+"F12.imprint","IMPRINT",EDGE,{"derivedFrom":subQ18}),-1.0]])]})]);}
            var Q1;
            Q1=makeQuery(id+"F5.boolean.opBoolean","SPLIT",FACE,{"disambiguationData":[TD([makeQuery(id+"F5.opExtrude","SWEPT_FACE",FACE,{"disambiguationData":[OSD([sQuery(id+"F4.wireOp",EDGE,"E41")])]})])],"derivedFrom":makeQuery(id+"F3.boolean.opBoolean","COPY",FACE,{"derivedFrom":makeQuery(id+"F3.opExtrude","CAP_FACE",FACE,{"disambiguationData":[OSD([sQuery(id+"F0.wireOp",EDGE,"E25.0"),sQuery(id+"F0.wireOp",EDGE,"E25.1"),sQuery(id+"F0.wireOp",EDGE,"E25.2"),sQuery(id+"F0.wireOp",EDGE,"E25.3"),sQuery(id+"F0.wireOp",EDGE,"E25.4"),sQuery(id+"F0.wireOp",EDGE,"E25.5"),sQuery(id+"F0.wireOp",EDGE,"E25.6"),sQuery(id+"F0.wireOp",EDGE,"E25.7")])],"isStart":false})})});
            extrude(context, id + "F13", {"entities" : qUnion([Q0]), "operationType" : NewBodyOperationType.REMOVE, "endBound" : BoundingType.UP_TO_SURFACE, "endBoundEntityFace" : qUnion([Q1]), "depth" : 25 * mm});
        }
        {
            var Q0;
            Q0=makeQuery(id+"F3.boolean.opBoolean","COPY",EDGE,{"derivedFrom":makeQuery(id+"F3.opExtrude","CAP_EDGE",EDGE,{"disambiguationData":[OSD([sQuery(id+"F0.wireOp",EDGE,"E25.6")])],"isStart":false})});
            var Q1;
            Q1=makeQuery(id+"F8.boolean.opBoolean","INTERSECT",EDGE,{"derivedFrom":[makeQuery(id+"F5.opExtrude","SWEPT_FACE",FACE,{"disambiguationData":[OSD([sQuery(id+"F4.wireOp",EDGE,"E30")])]}),makeQuery(id+"F8.opExtrude","CAP_FACE",FACE,{"disambiguationData":[OSD([sQuery(id+"F7.wireOp",EDGE,"E67")])],"isStart":false})]});
            var Q2;
            Q2=makeQuery(id+"F8.boolean.opBoolean","INTERSECT",EDGE,{"disambiguationData":[OD(1.0)],"derivedFrom":[makeQuery(id+"F5.opExtrude","SWEPT_FACE",FACE,{"disambiguationData":[OSD([sQuery(id+"F4.wireOp",EDGE,"E30")])]}),makeQuery(id+"F8.opExtrude","SWEPT_FACE",FACE,{"disambiguationData":[OSD([sQuery(id+"F7.wireOp",EDGE,"E67")])]})]});
            var Q3;
            {var subQ0=sQuery(id+"F4.wireOp",EDGE,"E30");Q3=makeQuery(id+"F8.boolean.opBoolean","SPLIT",EDGE,{"disambiguationData":[TD([makeQuery(id+"F5.opExtrude","SWEPT_FACE",FACE,{"disambiguationData":[OSD([sQuery(id+"F4.wireOp",EDGE,"E35.filletArc")])]})])],"derivedFrom":makeQuery(id+"F5.opExtrude","CAP_EDGE",EDGE,{"disambiguationData":[OSD([subQ0])],"isStart":false})});}
            var Q4;
            {var subQ0=sQuery(id+"F0.wireOp",EDGE,"E25.7");var subQ1=sQuery(id+"F0.wireOp",EDGE,"E25.1");var subQ2=sQuery(id+"F0.wireOp",EDGE,"E25.6");var subQ3=sQuery(id+"F0.wireOp",EDGE,"E25.5");var subQ4=sQuery(id+"F0.wireOp",EDGE,"E25.4");var subQ5=sQuery(id+"F0.wireOp",EDGE,"E25.0");var subQ6=sQuery(id+"F0.wireOp",EDGE,"E25.2");var subQ7=sQuery(id+"F0.wireOp",EDGE,"E25.3");Q4=makeQuery(id+"F8.boolean.opBoolean","INTERSECT",EDGE,{"derivedFrom":[makeQuery(id+"F5.boolean.opBoolean","SPLIT",FACE,{"disambiguationData":[TD([makeQuery(id+"F2.opExtrude","SWEPT_FACE",FACE,{"disambiguationData":[OSD([subQ5])]})])],"derivedFrom":makeQuery(id+"F3.boolean.opBoolean","COPY",FACE,{"derivedFrom":makeQuery(id+"F3.opExtrude","CAP_FACE",FACE,{"disambiguationData":[OSD([subQ5,subQ1,subQ6,subQ7,subQ4,subQ3,subQ2,subQ0])],"isStart":false})})}),makeQuery(id+"F8.opExtrude","SWEPT_FACE",FACE,{"disambiguationData":[OSD([sQuery(id+"F7.wireOp",EDGE,"E67")])]})]});}
            var Q5;
            Q5=makeQuery(id+"F8.boolean.opBoolean","INTERSECT",EDGE,{"disambiguationData":[OD(0.0)],"derivedFrom":[makeQuery(id+"F5.opExtrude","SWEPT_FACE",FACE,{"disambiguationData":[OSD([sQuery(id+"F4.wireOp",EDGE,"E30")])]}),makeQuery(id+"F8.opExtrude","SWEPT_FACE",FACE,{"disambiguationData":[OSD([sQuery(id+"F7.wireOp",EDGE,"E67")])]})]});
            fillet(context, id + "F14", {"entities" : qUnion([Q0, Q1, Q2, Q3, Q4, Q5]), "radius" : 3 * mm, "tangentPropagation" : true, "allowEdgeOverflow" : false});
        }
        {
            var Q0;
            Q0=makeQuery(id+"F1.opExtrude","CAP_EDGE",EDGE,{"disambiguationData":[OSD([sQuery(id+"F0.wireOp",EDGE,"E1.bottom")])],"isStart":false});
            fillet(context, id + "F15", {"entities" : qUnion([Q0]), "radius" : 2 * mm, "tangentPropagation" : true, "allowEdgeOverflow" : false});
        }
        {
            var Q0;
            {var subQ0=sQuery(id+"F0.wireOp",EDGE,"E21.filletArc");var subQ1=sQuery(id+"F0.wireOp",EDGE,"E7");var subQ2=sQuery(id+"F0.wireOp",EDGE,"E6");var subQ3=sQuery(id+"F0.wireOp",EDGE,"E5");var subQ4=sQuery(id+"F0.wireOp",EDGE,"E4");var subQ5=sQuery(id+"F0.wireOp",EDGE,"E22.filletArc");var subQ6=sQuery(id+"F0.wireOp",EDGE,"E1.bottom");var subQ7=sQuery(id+"F0.wireOp",EDGE,"E1.right");var subQ8=sQuery(id+"F0.wireOp",EDGE,"E1.top");var subQ9=sQuery(id+"F0.wireOp",EDGE,"E1.left");var subQ10=sQuery(id+"F0.wireOp",EDGE,"E23.filletArc");var subQ11=sQuery(id+"F0.wireOp",EDGE,"E24.filletArc");Q0=makeQuery(id+"F2.boolean.opBoolean","SPLIT",FACE,{"disambiguationData":[TD([makeQuery(id+"F1.opExtrude","SWEPT_FACE",FACE,{"disambiguationData":[OSD([subQ6])]})])],"derivedFrom":makeQuery(id+"F1.opExtrude","CAP_FACE",FACE,{"disambiguationData":[OSD([subQ6,subQ8,subQ9,subQ7,subQ4,subQ3,subQ2,subQ1,subQ0,subQ5,subQ10,subQ11])],"isStart":true})});}
            var sketch = newSketch(context, id + "F16", { "sketchPlane" : qUnion([Q0])});
            skLineSegment(sketch, "E79", {"start": v(0, 74.25) * mm, "end": v(0, 104.25) * mm, "construction": true});
            skCircle(sketch, "E80", {"center": v(0, 104.25) * mm, "radius": 6 * mm});
            skLineSegment(sketch, "E81", {"start": v(14.83, 104.25) * mm, "end": v(14.83, 92.25) * mm});
            skLineSegment(sketch, "E82", {"start": v(-15.17, 92.25) * mm, "end": v(-33.17, 74.25) * mm});
            skLineSegment(sketch, "E83", {"start": v(14.83, 92.25) * mm, "end": v(32.83, 74.25) * mm});
            skLineSegment(sketch, "E84", {"start": v(-15.17, 92.25) * mm, "end": v(-15.17, 104.25) * mm});
            skArc(sketch, "E85", {"start": v(14.83, 104.25) * mm, "mid": v(-0.17, 119.25) * mm, "end": v(-15.17, 104.25) * mm});
            skLineSegment(sketch, "E86", {"start": v(-80, 0) * mm, "end": v(80, 0) * mm, "construction": true});
            skLineSegment(sketch, "E87.MirrorCS", {"start": v(-14.83, 92.25) * mm, "end": v(-32.83, 74.25) * mm});
            skLineSegment(sketch, "E88.MirrorCS", {"start": v(-14.83, 104.25) * mm, "end": v(-14.83, 92.25) * mm});
            skLineSegment(sketch, "E89.MirrorCS", {"start": v(15.17, 92.25) * mm, "end": v(15.17, 104.25) * mm});
            skArc(sketch, "E90.MirrorCS", {"start": v(-14.83, 104.25) * mm, "mid": v(0.17, 119.25) * mm, "end": v(15.17, 104.25) * mm});
            skLineSegment(sketch, "E91.MirrorCS", {"start": v(14.83, -92.25) * mm, "end": v(32.83, -74.25) * mm});
            skLineSegment(sketch, "E92.MirrorCS", {"start": v(-15.17, -92.25) * mm, "end": v(-33.17, -74.25) * mm});
            skLineSegment(sketch, "E93.MirrorCS", {"start": v(-15.17, -92.25) * mm, "end": v(-15.17, -104.25) * mm});
            skCircle(sketch, "E94.MirrorC", {"center": v(0, -104.25) * mm, "radius": 6 * mm});
            skLineSegment(sketch, "E95.MirrorCS", {"start": v(14.83, -104.25) * mm, "end": v(14.83, -92.25) * mm});
            skLineSegment(sketch, "E96.MirrorCS", {"start": v(0, -74.25) * mm, "end": v(0, -104.25) * mm, "construction": true});
            skArc(sketch, "E97", {"start": v(-15.17, -104.25) * mm, "mid": v(-0.17, -119.25) * mm, "end": v(14.83, -104.25) * mm});
            skSolve(sketch);
        }
        {
            var Q0;
            {var subQ2=sQuery(id+"F16.wireOp",EDGE,"E81");Q0=makeQuery(id+"F16.imprint","IMPRINT",FACE,{"disambiguationData":[TD([[makeQuery(id+"F16.imprint","IMPRINT",EDGE,{"derivedFrom":subQ2}),-1.0]])]});}
            var Q1;
            Q1=makeQuery(id+"F16.imprint","IMPRINT",FACE,{"disambiguationData":[TD([[makeQuery(id+"F16.imprint","IMPRINT",EDGE,{"derivedFrom":makeQuery(id+"F1.opExtrude","CAP_EDGE",EDGE,{"disambiguationData":[OSD([sQuery(id+"F0.wireOp",EDGE,"E1.left")])],"isStart":true})}),-1.0]])]});
            var Q2;
            {var subQ1=sQuery(id+"F16.wireOp",EDGE,"E91.MirrorCS");Q2=makeQuery(id+"F16.imprint","IMPRINT",FACE,{"disambiguationData":[TD([[makeQuery(id+"F16.imprint","IMPRINT",EDGE,{"derivedFrom":subQ1}),1.0]])]});}
            var Q3;
            Q3=makeQuery(id+"F2.opExtrude","CAP_FACE",FACE,{"disambiguationData":[OSD([sQuery(id+"F0.wireOp",EDGE,"E12"),sQuery(id+"F0.wireOp",EDGE,"E13"),sQuery(id+"F0.wireOp",EDGE,"E14"),sQuery(id+"F0.wireOp",EDGE,"E15"),sQuery(id+"F0.wireOp",EDGE,"E17.filletArc"),sQuery(id+"F0.wireOp",EDGE,"E18.filletArc"),sQuery(id+"F0.wireOp",EDGE,"E19.filletArc"),sQuery(id+"F0.wireOp",EDGE,"E20.filletArc"),sQuery(id+"F0.wireOp",EDGE,"E25.0"),sQuery(id+"F0.wireOp",EDGE,"E25.1"),sQuery(id+"F0.wireOp",EDGE,"E25.2"),sQuery(id+"F0.wireOp",EDGE,"E25.3"),sQuery(id+"F0.wireOp",EDGE,"E25.4"),sQuery(id+"F0.wireOp",EDGE,"E25.5"),sQuery(id+"F0.wireOp",EDGE,"E25.6"),sQuery(id+"F0.wireOp",EDGE,"E25.7")])],"isStart":false});
            extrude(context, id + "F17", {"entities" : qUnion([Q0, Q1, Q2]), "endBound" : BoundingType.UP_TO_SURFACE, "endBoundEntityFace" : qUnion([Q3]), "depth" : 25 * mm});
        }
    });
